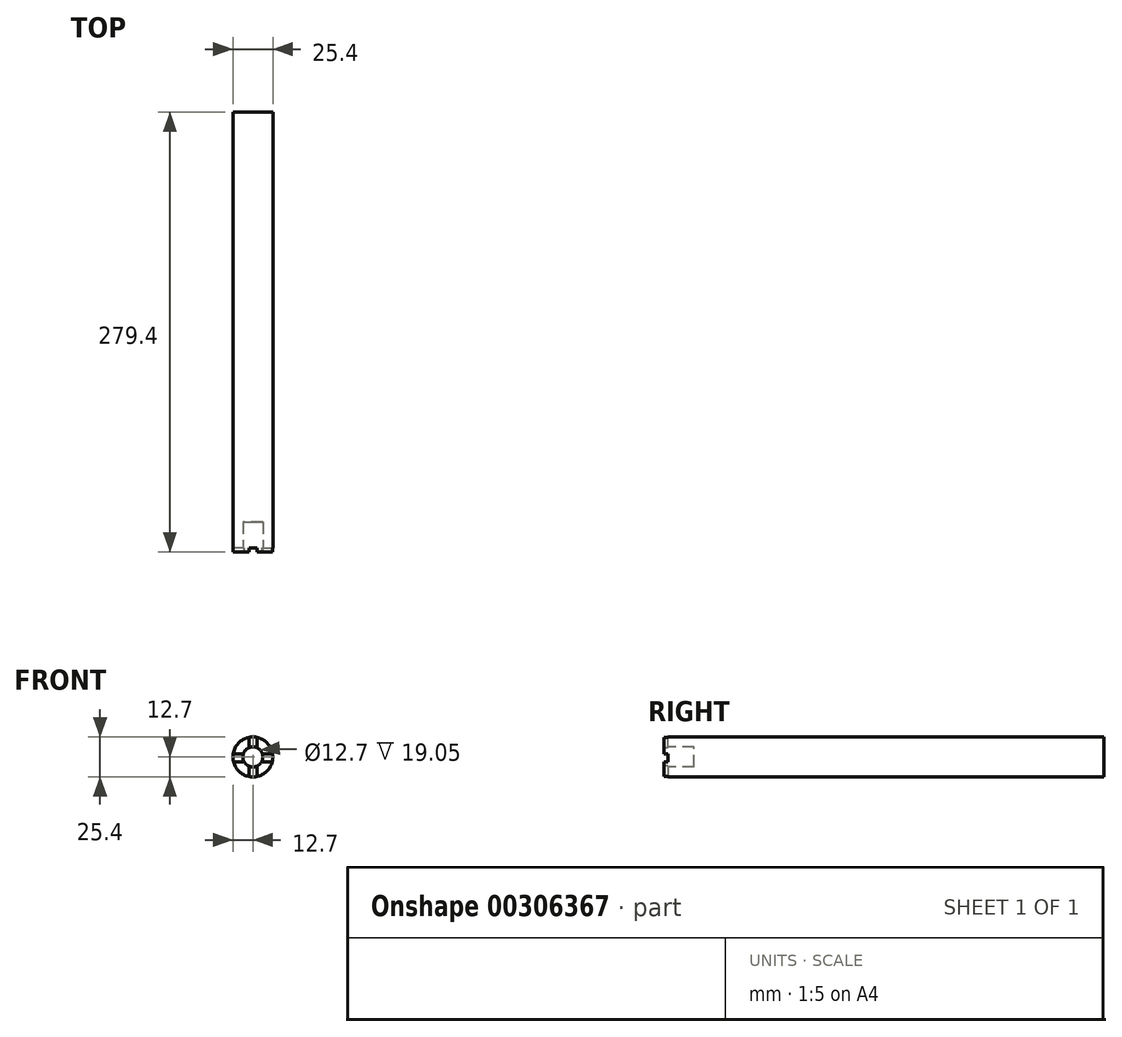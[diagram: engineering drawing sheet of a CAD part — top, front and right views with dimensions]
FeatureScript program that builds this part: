
annotation { "Feature Type Name" : "Feature", "Feature Type Description" : "" }
export const myFeature = defineFeature(function(context is Context, id is Id, definition is map)
    precondition{}
    {
        {
            var Q0;
            Q0=qCreatedBy(makeId("Front.planeOp"),FACE);
            var sketch = newSketch(context, id + "F0", { "sketchPlane" : qUnion([Q0])});
            skCircle(sketch, "E0", {"center": v(0, 0) * mm, "radius": 12.7 * mm});
            skSolve(sketch);
        }
        {
            var Q0;
            Q0 = qSketchRegion(id + "F0", true);
            extrude(context, id + "F1", {"entities" : qUnion([Q0]), "depth" : 279.4 * mm});
        }
        {
            var Q0;
            Q0=makeQuery(id+"F1.opExtrude","CAP_FACE",FACE,{"disambiguationData":[OSD([sQuery(id+"F0.wireOp",EDGE,"E0")])],"isStart":false});
            var sketch = newSketch(context, id + "F2", { "sketchPlane" : qUnion([Q0])});
            skCircle(sketch, "E1", {"center": v(0, 0) * mm, "radius": 6.35 * mm});
            skLineSegment(sketch, "E2.0", {"start": v(-2.54, 5.82) * mm, "end": v(-2.54, 12.44) * mm});
            skLineSegment(sketch, "E3.0", {"start": v(2.54, 5.82) * mm, "end": v(2.54, 12.44) * mm});
            skLineSegment(sketch, "E4", {"start": v(6.03, 2) * mm, "end": v(12.54, 2) * mm});
            skLineSegment(sketch, "E5", {"start": v(5.55, -3.08) * mm, "end": v(12.32, -3.08) * mm});
            skLineSegment(sketch, "E6.trimOffspring", {"start": v(-6.03, 2) * mm, "end": v(-12.54, 2) * mm});
            skLineSegment(sketch, "E7.trimOffspring", {"start": v(-5.55, -3.08) * mm, "end": v(-12.32, -3.08) * mm});
            skLineSegment(sketch, "E8.trimOffspring", {"start": v(-2.54, -5.82) * mm, "end": v(-2.54, -12.44) * mm});
            skLineSegment(sketch, "E9.trimOffspring", {"start": v(2.54, -5.82) * mm, "end": v(2.54, -12.44) * mm});
            skSolve(sketch);
        }
        {
            var Q0;
            {var subQ0=sQuery(id+"F2.wireOp",EDGE,"E6.trimOffspring");Q0=makeQuery(id+"F2.imprint","IMPRINT",FACE,{"disambiguationData":[TD([[makeQuery(id+"F2.imprint","IMPRINT",EDGE,{"derivedFrom":subQ0}),1.0]])]});}
            var Q1;
            {var subQ0=sQuery(id+"F2.wireOp",EDGE,"E2.0");Q1=makeQuery(id+"F2.imprint","IMPRINT",FACE,{"disambiguationData":[TD([[makeQuery(id+"F2.imprint","IMPRINT",EDGE,{"derivedFrom":subQ0}),-1.0]])]});}
            var Q2;
            {var subQ0=sQuery(id+"F2.wireOp",EDGE,"E4");Q2=makeQuery(id+"F2.imprint","IMPRINT",FACE,{"disambiguationData":[TD([[makeQuery(id+"F2.imprint","IMPRINT",EDGE,{"derivedFrom":subQ0}),-1.0]])]});}
            var Q3;
            {var subQ0=sQuery(id+"F2.wireOp",EDGE,"E8.trimOffspring");Q3=makeQuery(id+"F2.imprint","IMPRINT",FACE,{"disambiguationData":[TD([[makeQuery(id+"F2.imprint","IMPRINT",EDGE,{"derivedFrom":subQ0}),1.0]])]});}
            extrude(context, id + "F3", {"entities" : qUnion([Q0, Q1, Q2, Q3]), "operationType" : NewBodyOperationType.REMOVE, "oppositeDirection" : true, "depth" : 2.54 * mm});
        }
        {
            var Q0;
            {var subQ0=sQuery(id+"F2.wireOp",EDGE,"E1");var subQ4=makeQuery(id+"F2.imprint","INTERSECT",VERTEX,{"derivedFrom":[subQ0,sQuery(id+"F2.wireOp",EDGE,"E3.0")]});Q0=makeQuery(id+"F2.imprint","IMPRINT",FACE,{"disambiguationData":[TD([[makeQuery(id+"F2.imprint","IMPRINT",EDGE,{"disambiguationData":[TD([[subQ4,1.0]])],"derivedFrom":subQ0}),1.0]])]});}
            extrude(context, id + "F4", {"entities" : qUnion([Q0]), "operationType" : NewBodyOperationType.REMOVE, "oppositeDirection" : true, "depth" : 19.05 * mm});
        }
    });
